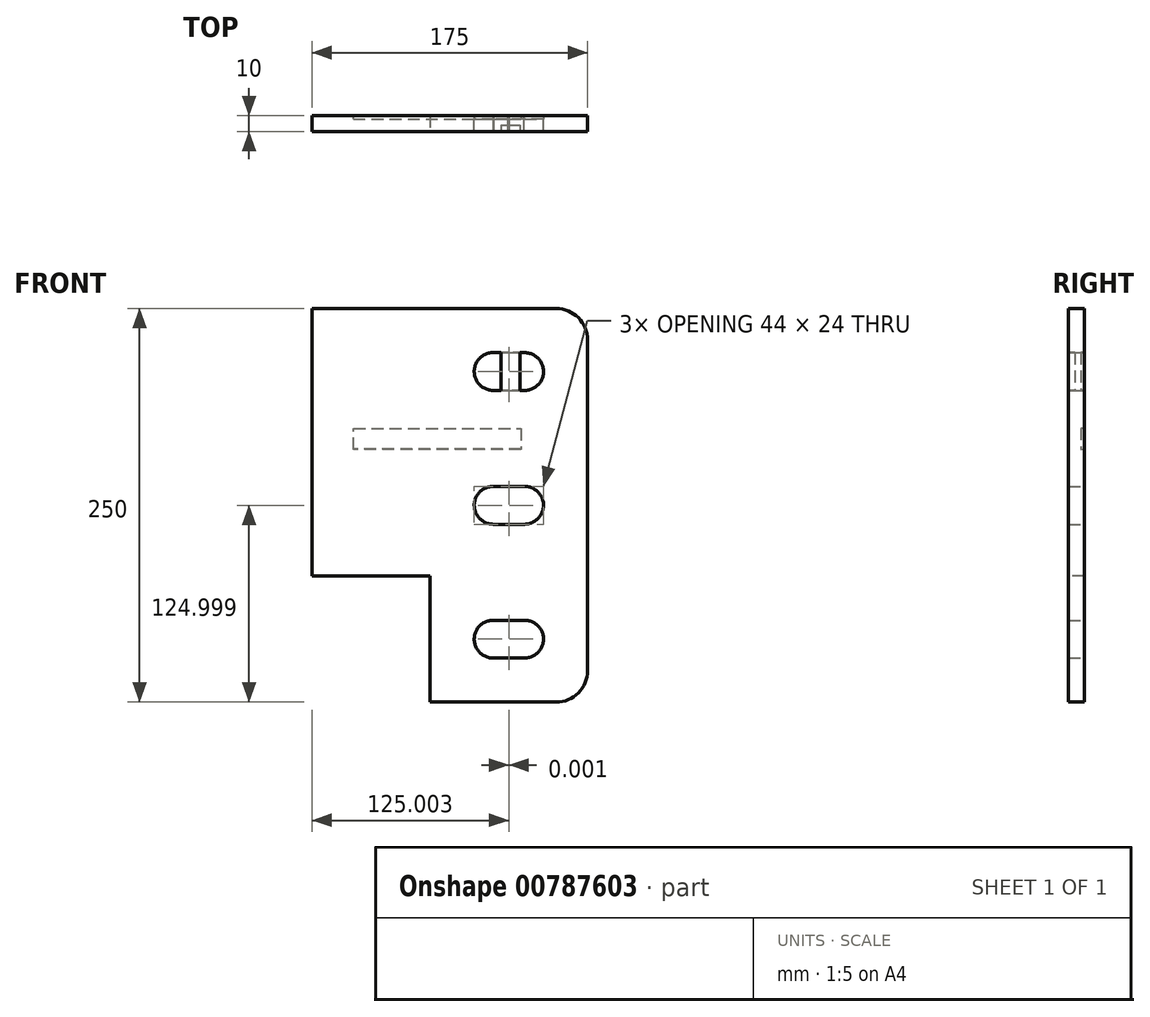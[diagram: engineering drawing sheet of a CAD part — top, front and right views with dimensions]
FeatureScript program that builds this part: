
annotation { "Feature Type Name" : "Feature", "Feature Type Description" : "" }
export const myFeature = defineFeature(function(context is Context, id is Id, definition is map)
    precondition{}
    {
        {
            var Q0;
            Q0=qCreatedBy(makeId("Front.planeOp"),FACE);
            var sketch = newSketch(context, id + "F0", { "sketchPlane" : qUnion([Q0])});
            skLineSegment(sketch, "E0.bottom", {"start": v(2261.52, -2930.47) * mm, "end": v(2416.52, -2930.47) * mm});
            skLineSegment(sketch, "E0.top", {"start": v(2261.52, -3180.47) * mm, "end": v(2416.52, -3180.47) * mm});
            skLineSegment(sketch, "E0.left", {"start": v(2261.52, -2930.47) * mm, "end": v(2261.52, -3180.47) * mm});
            skLineSegment(sketch, "E0.right", {"start": v(2436.52, -2950.47) * mm, "end": v(2436.52, -3160.47) * mm});
            skPoint(sketch, "E1.visualSharp", {"position": v(2436.52, -2930.47) * mm});
            skArc(sketch, "E1.filletArc", {"start": v(2436.52, -2950.47) * mm, "mid": v(2430.67, -2936.33) * mm, "end": v(2416.52, -2930.47) * mm});
            skPoint(sketch, "E2.visualSharp", {"position": v(2436.52, -3180.47) * mm});
            skArc(sketch, "E2.filletArc", {"start": v(2416.52, -3180.47) * mm, "mid": v(2430.67, -3174.61) * mm, "end": v(2436.52, -3160.47) * mm});
            skLineSegment(sketch, "E3", {"start": v(2386.52, -2930.47) * mm, "end": v(2386.52, -3180.47) * mm, "construction": true});
            skCircle(sketch, "E4", {"center": v(2386.52, -3055.47) * mm, "radius": 12 * mm});
            skCircle(sketch, "E5", {"center": v(2386.52, -2970.47) * mm, "radius": 12 * mm});
            skCircle(sketch, "E6", {"center": v(2386.52, -3140.47) * mm, "radius": 12 * mm});
            skCircle(sketch, "E7", {"center": v(2376.52, -2970.47) * mm, "radius": 12 * mm});
            skCircle(sketch, "E8", {"center": v(2396.52, -2970.47) * mm, "radius": 12 * mm});
            skLineSegment(sketch, "E9", {"start": v(2376.4, -2958.47) * mm, "end": v(2396.52, -2958.47) * mm});
            skLineSegment(sketch, "E10", {"start": v(2375.94, -2982.46) * mm, "end": v(2396.91, -2982.46) * mm});
            skLineSegment(sketch, "E11", {"start": v(2386.52, -3055.47) * mm, "end": v(2534.86, -3055.47) * mm, "construction": true});
            skLineSegment(sketch, "E12.MirrorCS", {"start": v(2375.94, -3128.49) * mm, "end": v(2396.91, -3128.48) * mm});
            skLineSegment(sketch, "E13.MirrorCS", {"start": v(2376.4, -3152.47) * mm, "end": v(2396.52, -3152.47) * mm});
            skCircle(sketch, "E14.MirrorC", {"center": v(2376.52, -3140.47) * mm, "radius": 12 * mm});
            skCircle(sketch, "E15.MirrorC", {"center": v(2396.52, -3140.47) * mm, "radius": 12 * mm});
            skCircle(sketch, "E16", {"center": v(2376.52, -3055.47) * mm, "radius": 12 * mm});
            skCircle(sketch, "E17", {"center": v(2396.52, -3055.47) * mm, "radius": 12 * mm});
            skLineSegment(sketch, "E18", {"start": v(2376.5, -3043.47) * mm, "end": v(2397.07, -3043.48) * mm});
            skLineSegment(sketch, "E19", {"start": v(2376.3, -3067.47) * mm, "end": v(2396.52, -3067.47) * mm});
            skSolve(sketch);
        }
        {
            var Q0;
            Q0 = qSketchRegion(id + "F0", true);
            extrude(context, id + "F1", {"entities" : qUnion([Q0]), "depth" : 10 * mm, "offsetDistance" : 25 * mm});
        }
        {
            var Q0;
            Q0=makeQuery(id+"F1.opExtrude","CAP_FACE",FACE,{"disambiguationData":[OSD([sQuery(id+"F0.wireOp",EDGE,"E0.bottom"),sQuery(id+"F0.wireOp",EDGE,"E0.top"),sQuery(id+"F0.wireOp",EDGE,"E0.left"),sQuery(id+"F0.wireOp",EDGE,"E0.right"),sQuery(id+"F0.wireOp",EDGE,"E1.filletArc"),sQuery(id+"F0.wireOp",EDGE,"E2.filletArc"),sQuery(id+"F0.wireOp",EDGE,"E4"),sQuery(id+"F0.wireOp",EDGE,"E5"),sQuery(id+"F0.wireOp",EDGE,"E7"),sQuery(id+"F0.wireOp",EDGE,"E8"),sQuery(id+"F0.wireOp",EDGE,"E9"),sQuery(id+"F0.wireOp",EDGE,"E10"),sQuery(id+"F0.wireOp",EDGE,"E12.MirrorCS"),sQuery(id+"F0.wireOp",EDGE,"E13.MirrorCS"),sQuery(id+"F0.wireOp",EDGE,"E14.MirrorC"),sQuery(id+"F0.wireOp",EDGE,"E6"),sQuery(id+"F0.wireOp",EDGE,"E15.MirrorC"),sQuery(id+"F0.wireOp",EDGE,"E16"),sQuery(id+"F0.wireOp",EDGE,"E17"),sQuery(id+"F0.wireOp",EDGE,"E18"),sQuery(id+"F0.wireOp",EDGE,"E19")])],"isStart":false});
            var sketch = newSketch(context, id + "F2", { "sketchPlane" : qUnion([Q0])});
            skLineSegment(sketch, "E20.bottom", {"start": v(2261.52, -3180.47) * mm, "end": v(2336.52, -3180.47) * mm});
            skLineSegment(sketch, "E20.top", {"start": v(2261.52, -3100.47) * mm, "end": v(2336.52, -3100.47) * mm});
            skLineSegment(sketch, "E20.left", {"start": v(2261.52, -3180.47) * mm, "end": v(2261.52, -3100.47) * mm});
            skLineSegment(sketch, "E20.right", {"start": v(2336.52, -3180.47) * mm, "end": v(2336.52, -3100.47) * mm});
            skSolve(sketch);
        }
        {
            var Q0;
            Q0 = qSketchRegion(id + "F2", true);
            extrude(context, id + "F3", {"entities" : qUnion([Q0]), "operationType" : NewBodyOperationType.REMOVE, "oppositeDirection" : true, "depth" : 25 * mm, "offsetDistance" : 25 * mm});
        }
        {
            var Q0;
            Q0=makeQuery(id+"F1.opExtrude","CAP_FACE",FACE,{"disambiguationData":[OSD([sQuery(id+"F0.wireOp",EDGE,"E0.bottom"),sQuery(id+"F0.wireOp",EDGE,"E0.top"),sQuery(id+"F0.wireOp",EDGE,"E0.left"),sQuery(id+"F0.wireOp",EDGE,"E0.right"),sQuery(id+"F0.wireOp",EDGE,"E1.filletArc"),sQuery(id+"F0.wireOp",EDGE,"E2.filletArc"),sQuery(id+"F0.wireOp",EDGE,"E4"),sQuery(id+"F0.wireOp",EDGE,"E5"),sQuery(id+"F0.wireOp",EDGE,"E7"),sQuery(id+"F0.wireOp",EDGE,"E8"),sQuery(id+"F0.wireOp",EDGE,"E9"),sQuery(id+"F0.wireOp",EDGE,"E10"),sQuery(id+"F0.wireOp",EDGE,"E12.MirrorCS"),sQuery(id+"F0.wireOp",EDGE,"E13.MirrorCS"),sQuery(id+"F0.wireOp",EDGE,"E14.MirrorC"),sQuery(id+"F0.wireOp",EDGE,"E6"),sQuery(id+"F0.wireOp",EDGE,"E15.MirrorC"),sQuery(id+"F0.wireOp",EDGE,"E16"),sQuery(id+"F0.wireOp",EDGE,"E17"),sQuery(id+"F0.wireOp",EDGE,"E18"),sQuery(id+"F0.wireOp",EDGE,"E19")])],"isStart":false});
            var sketch = newSketch(context, id + "F4", { "sketchPlane" : qUnion([Q0])});
            skPoint(sketch, "E21.firstSnap0", {"position": v(2381.54, -2958.47) * mm});
            skLineSegment(sketch, "E21.bottom", {"start": v(2381.54, -2948.3) * mm, "end": v(2393.48, -2948.3) * mm});
            skLineSegment(sketch, "E21.top", {"start": v(2381.54, -2993.93) * mm, "end": v(2393.48, -2993.93) * mm});
            skLineSegment(sketch, "E21.left", {"start": v(2381.54, -2948.3) * mm, "end": v(2381.54, -2993.93) * mm});
            skLineSegment(sketch, "E21.right", {"start": v(2393.48, -2948.3) * mm, "end": v(2393.48, -2993.93) * mm});
            skSolve(sketch);
        }
        {
            var Q0;
            Q0 = qSketchRegion(id + "F4", true);
            extrude(context, id + "F5", {"entities" : qUnion([Q0]), "operationType" : NewBodyOperationType.ADD, "oppositeDirection" : true, "depth" : 4 * mm, "offsetDistance" : 25 * mm});
        }
        {
            var Q0;
            Q0=makeQuery(id+"F1.opExtrude","CAP_FACE",FACE,{"disambiguationData":[OSD([sQuery(id+"F0.wireOp",EDGE,"E0.bottom"),sQuery(id+"F0.wireOp",EDGE,"E0.top"),sQuery(id+"F0.wireOp",EDGE,"E0.left"),sQuery(id+"F0.wireOp",EDGE,"E0.right"),sQuery(id+"F0.wireOp",EDGE,"E1.filletArc"),sQuery(id+"F0.wireOp",EDGE,"E2.filletArc"),sQuery(id+"F0.wireOp",EDGE,"E4"),sQuery(id+"F0.wireOp",EDGE,"E5"),sQuery(id+"F0.wireOp",EDGE,"E7"),sQuery(id+"F0.wireOp",EDGE,"E8"),sQuery(id+"F0.wireOp",EDGE,"E9"),sQuery(id+"F0.wireOp",EDGE,"E10"),sQuery(id+"F0.wireOp",EDGE,"E12.MirrorCS"),sQuery(id+"F0.wireOp",EDGE,"E13.MirrorCS"),sQuery(id+"F0.wireOp",EDGE,"E14.MirrorC"),sQuery(id+"F0.wireOp",EDGE,"E6"),sQuery(id+"F0.wireOp",EDGE,"E15.MirrorC"),sQuery(id+"F0.wireOp",EDGE,"E16"),sQuery(id+"F0.wireOp",EDGE,"E17"),sQuery(id+"F0.wireOp",EDGE,"E18"),sQuery(id+"F0.wireOp",EDGE,"E19")])],"isStart":true});
            var sketch = newSketch(context, id + "F6", { "sketchPlane" : qUnion([Q0])});
            skLineSegment(sketch, "E22.bottom", {"start": v(-2394.1, -3006.64) * mm, "end": v(-2287.94, -3006.64) * mm});
            skLineSegment(sketch, "E22.top", {"start": v(-2394.1, -3019.8) * mm, "end": v(-2287.94, -3019.8) * mm});
            skLineSegment(sketch, "E22.left", {"start": v(-2394.1, -3006.64) * mm, "end": v(-2394.1, -3019.8) * mm});
            skLineSegment(sketch, "E22.right", {"start": v(-2287.94, -3006.64) * mm, "end": v(-2287.94, -3019.8) * mm});
            skSolve(sketch);
        }
        {
            var Q0;
            Q0 = qSketchRegion(id + "F6", true);
            var Q1;
            {var subQ1=sQuery(id+"F0.wireOp",EDGE,"E7");Q1=makeQuery(id+"F6.imprint","IMPRINT",FACE,{"disambiguationData":[TD([[makeQuery(id+"F6.imprint","IMPRINT",EDGE,{"derivedFrom":makeQuery(id+"F1.opExtrude","CAP_EDGE",EDGE,{"disambiguationData":[OSD([subQ1])],"isStart":true})}),-1.0]])]});}
            extrude(context, id + "F7", {"entities" : qUnion([Q0, Q1]), "operationType" : NewBodyOperationType.REMOVE, "depth" : -2.2 * mm, "offsetDistance" : 25 * mm, "hasDraft" : true, "draftAngle" : 3 * degree});
        }
    });
